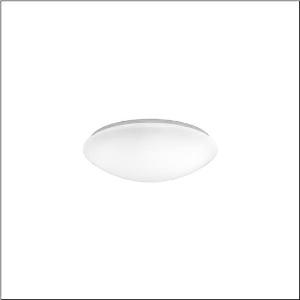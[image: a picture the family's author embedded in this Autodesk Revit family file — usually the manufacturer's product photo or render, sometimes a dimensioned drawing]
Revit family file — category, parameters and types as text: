
# Revit family: round_31_b_5pja030001a
name_source: partatom
category: Lighting Fixtures
units: mm (PartAtom-declared; Revit-internal decimal feet)

## family parameters
Cut with Voids When Loaded = No
Host = Face
Light Source = No
Part Type = Normal
Room Calculation Point = No
Round Connector Dimension = Use Diameter
Shared = No

## types (1)
- Round 31 B (1 x LED, 1900 lm, 15 W, 4000K)
    Apparent Load = 15 VA
    CIE Flux Codes = 42 71 89 88 100
    Color Rendering = 80
    Color Temperature = 4000K
    Default Elevation = 1800 mm
    Description = Round 31 B, wall and ceiling luminaire, primary optical cover: enclosure, of PMMA, light emission: direct distribution, primary light characteristic: symmetric, installation type: surface-mounted, LED, rated luminous flux: 1.900lm, luminous efficacy: 126lm/W, light colour: 840, colour temperature: 4000K, with terminal, 3-pole, max. 2.5mm², mains connection: 230V, AC, 50/60Hz, rated input power: 15W, luminaire housing, round, of steel, white, diameter: 290mm, height: 85mm, protection rating (complete): IP40, insulation class (complete): insulation class I (protective earthing), certification: CE, impact resistance: IK02, packaging unit: 1 piece
    Height = 85 mm
    Lamp = 1 x LED
    Lamp Light Flux = 1900 lm
    Lamp Power = 15 W
    Lamp count = 1
    Length = 290 mm
    Luminous efficacy = 127 lm/W
    Manufacturer = Siteco
    ModVariant = No
    Model = 5PJA030001A
    Mounting Place = Ceiling
    Mounting Type = Surface mounted
    Number of Poles = 1
    OnlyDefault = Yes
    Power Factor = 1
    Product Name = Round 31 B
    Product group = wall and ceiling luminaire
    ProductGroupID = 302
    Protection Class = Protection class I
    Protection Degree = IP 40
    RLX_Detail_Level = 1
    RLX_Emergency_Light_Flux = 0 lm
    RLX_Emergency_Type = 0
    RLX_Emergency_Type_DB = No
    RlxData = <blob elided: 9181 chars, md5=6f685ec4>
    Socket = socket
    Standby Power = 0 W
    System Light Flux = 1900 lm
    System Power = 15 W
    Type Comments = Product without accessories
    Type Image = l_1258346.jpg
    URL = http://relux.com
    VarID = ---
    Voltage = 0 V
    Weight = 0.00 kg
    Width = 0 mm  [stored 0 ft]

note: [stored X ft] marks values corroborated as IEEE doubles in the binary element streams (Revit-internal decimal feet)

## geometry (parser evidence)
native form markers: Sweep x10
no freeform markers — native parametric forms only
